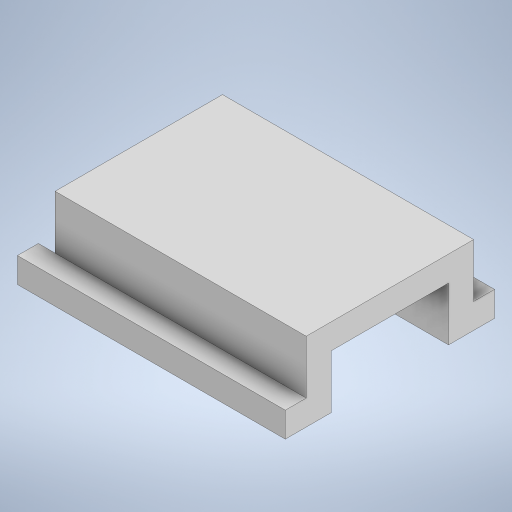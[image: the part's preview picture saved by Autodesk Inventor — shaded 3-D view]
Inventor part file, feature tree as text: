
AUTODESK INVENTOR PART (.ipt)
format: ipt  version: 2024 (Build 280153000, 153)  size: 240,640 bytes
history: native  units: mm
features: extrude x3, sketch x3
ambient origin geometry x8: Origin, YZ Plane, XZ Plane, XY Plane, X Axis, Y Axis, Z Axis, Center Point
bodies: Solid1 (feature_tree)
feature tree (6):
  extrude  "Extrusion1"  Depth=150.0mm
  extrude  "Extrusion2"  Depth=15.0mm
  extrude  "Extrusion3"  Depth=15.0mm
  sketch  "Sketch1"  dims[d0=100.0mm d1=150.0mm]
  sketch  "Sketch2"  dims[d2=47.0mm d3=0.0mm d4=15.0mm]
  sketch  "Sketch3"  dims[d5=15.0mm d6=15.0mm d7=200.0mm d8=0.0mm d9=12.5mm d10=12.5mm d11=15.0mm d12=15.0mm d13=160.0mm d14=0.0mm]
